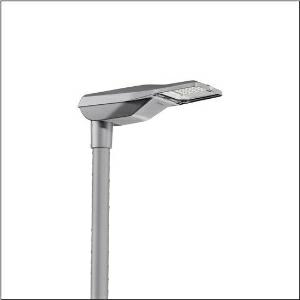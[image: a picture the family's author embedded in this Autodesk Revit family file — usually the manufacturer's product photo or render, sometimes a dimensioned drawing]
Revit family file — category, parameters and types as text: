
# Revit family: streetlight_sl_21_iq_micro___stw1_0a_5xe1e61d08cb_4749
name_source: partatom
category: Lighting Fixtures
units: mm (PartAtom-declared; Revit-internal decimal feet)

## family parameters
Cut with Voids When Loaded = No
Host = Face
Light Source = No
Part Type = Normal
Room Calculation Point = No
Round Connector Dimension = Use Diameter
Shared = No

## types (1)
- --- (1 x LED, 2570 lm, 19.4 W, 2700K)
    Apparent Load = 19 VA
    CIE Flux Codes = 38 75 98 100 100
    Color Rendering = 70
    Color Temperature = 2700K
    Default Elevation = 1800 mm
    Description = Streetlight SL 21 iQ micro, mast luminaire, primary light control with lens, of PMMA, primary optical cover: cover, of toughened safety glass, transparent, light distribution: STW1.0a, light emission: direct distribution, primary light characteristic: asymmetric, installation type: post-top, side-entry, LED, High Power LED, rated luminous flux: 2.570lm, luminous efficacy: 133lm/W, light colour: 727, colour temperature: 2700K, control gear: iQ-Comfort, control: Auto-Match, Temp-Guard, Lumen-Switch, Night-Set, Smart-Wire, Light-Fading, Desk-Remote (wireless, voltage-free reading and setting of iQ features in the workshop via application-optimized NFC function/RFID function), optimised constant luminous flux control (CLO 2.0), pre-setting: linear dimming characteristic, mains connection: 220..240V, AC, 50/60Hz, start of lifetime: 19W, end of service life: 20W, reduction: 10W, luminaire housing, of diecast aluminium, powder-coated, Siteco® metallic grey (DB 702S), corrosivity category C5 mid according to DIN EN ISO 12944, please order mast flange separately, inclination adjustable: 0°, 5°, 10°, 15°, sealing non-destructively replaceable, multi-level sealing system, length: 528mm, width: 235mm, height: 110mm, mast flange for spigot size: 42mm (side-entry): 5XC10008XM4, 60/48mm (side-entry/post-top): 5XC10108XM2, 76/60mm (side-entry/post-top): 5XC10108XM1, protection rating (complete): IP66, insulation class (complete): insulation class II (safety insulation), certification: CE, ENEC, ENEC+, VDE, impact resistance: IK10, permissible operating ambient temperature for outdoor applications: -40..+50°C, standard-compliant lighting for roads and squares, packaging unit: 1 piece

Light Distribution: STW1.0a
    Height = 110 mm
    Lamp = 1 x LED
    Lamp Light Flux = 2570 lm
    Lamp Power = 19.4 W
    Lamp count = 1
    Length = 528 mm
    Luminous efficacy = 132 lm/W
    Manufacturer = Siteco
    ModVariant = No
    Model = 5XE1E61D08CB
    Number of Poles = 1
    OnlyDefault = Yes
    Power Factor = 1
    Product Name = Streetlight SL 21 iQ micro | STW1.0a
    Product group = mast luminaire | pylon top
    ProductGroupID = 6100
    Protection Class = Protection class II
    Protection Degree = IP 66
    RLX_Detail_Level = 1
    RLX_Emergency_Light_Flux = 0 lm
    RLX_Emergency_Type = 0
    RLX_Emergency_Type_DB = No
    RlxData = <blob elided: 99741 chars, md5=db14f85c>
    Socket = socket
    Standby Power = 0 W
    System Light Flux = 2570 lm
    System Power = 19 W
    Type Comments = factory setting: luminous flux: 100 % | dim-lin: 254 | 387 mA
    Type Image = l_1006881.jpg
    URL = http://relux.com
    VarID = @adj_160231
    Voltage = 0 V
    Weight = 0.00 kg
    Width = 235 mm

## geometry (parser evidence)
native form markers: Blend x4, Sweep x11
no freeform markers — native parametric forms only
